# Revit family: ONRB - 1-6 door - All
name_source: partatom
category: Mechanical Equipment
units: mm (PartAtom-declared; Revit-internal decimal feet)

## family parameters
Always vertical = Yes
Cut with Voids When Loaded = No
OmniClass Number = 23.40.40.11.17
OmniClass Title = Refrigerated Cases
Part Type = Normal
Room Calculation Point = No
Round Connector Dimension = Use Radius
Shared = No
Work Plane-Based = Yes

## types (10) — shared parameters
20" Shelf = No
22" Shelf = Yes
Application Discipline = Beverage
BTUH Conventional = 549
BTUH Parallel = 519
Certifications = NSF 7, UL471, CSA
DATE = 01/29/2016
Default Elevation = 48"
Defrosts Per Day_2 = 4
Description = Narrow Reach-In Merchandiser
Discharge Air (°F) = 38 °F
Discharge Air Velocity (FPM) = 380 (FPM)
EQUIPMENT DESCRIPTION = Narrow Reach-In Merchandiser
EQUIPMENT MARK = ONRB
Evaporator (°F) = 34 °F
GLASS = Glass
Height = 81"
Item Description = Narrow Reach-In Merchandiser
Keynote = ONRB
Legend Number = ONRB
Manufacturer = HILL PHOENIX
Model = ONRB
NUMBER FOR GUIDLINES AND CONTROL ORGANIZATION = 1
PAINTED METAL EXTERIOR = CHARCOAL BROWN
Size of Door = 30"
Solid End LH = Yes
Superheat Set Point @ Bulb (°F) = 6-8 °F
Timed-Off Defrost Fail-Safe (Min) = 30 (Min)
Timed-Off Defrost Termination Temp_2 = 47°F
Type of Door Swing = A-Swing
URL = http://www.hillphoenix.com
Vista Optimax Pro Amps = 0 A
Vista Optimax Pro Watts = 0 W
Width = 34 7/8"
zero-valued in all types: NUMBER FOR ELECTRICAL DATA

## per-type parameters (varying)
| type | 101 Amps | 101 Watts | CENTER LINE & DRAIN | Crossfire/Polaris Amps | Crossfire/Polaris Watts | DOOR CONFIGURATION | Eliminaator Amps | Eliminaator Watts | GE Immersion Amps | GE Immersion Watts | High Efficiency Amps | High Efficiency Watts | Length | NUMBER FOR LIGHTING DATA | NUMBER OF DOORS | Number of Fans per Case | Optimax Pro Amps | Optimax Pro Watts | Solid End LH1 | Solid End RH | Solid End RH1 | Vista-C/60 Amps | Vista-C/60 Watts |
| 5 Door - Beverage | 1 A | 127 W | 90" | 1 A | 90 W | MASTER DOOR : 30" X 64 3/8" 6 DOOR A SWING (LEFT OPENING) | 1 A | 127 W | 1 A | 96 W | 1 A | 158 W | 180" | 6 | 6 | 6 | 1 A | 61 W | No | Yes | No | 1 A | 135 W |
| 6 Door - Beverage | 1 A | 127 W | 90" | 1 A | 90 W | MASTER DOOR : 30" X 64 3/8" 6 DOOR A SWING (LEFT OPENING) | 1 A | 127 W | 1 A | 96 W | 1 A | 158 W | 180" | 6 | 6 | 6 | 1 A | 61 W | Yes | No | Yes | 1 A | 135 W |
| 1 Door - Beverage | 0 A | 19 W | 15 1/2" | 0 A | 15 W | MASTER DOOR : 31" X 64 3/8" 1 DOOR A SWING (LEFT OPENING) | 0 A | 19 W | 0 A | 16 W | 0 A | 26 W | 31" | 1 | 1 | 1 | 0 A | 10 W | No | Yes | No | 0 A | 24 W |
| 2 DR | 0 A | 19 W | 30" | 0 A | 15 W | MASTER DOOR : 30" X 64 3/8" 2 DOOR A SWING (LEFT OPENING) | 0 A | 19 W | 0 A | 16 W | 0 A | 26 W | 60" | 1 | 1 | 1 | 0 A | 10 W | No | Yes | No | 0 A | 24 W |
| 3DR | 0 A | 19 W | 45" | 0 A | 15 W | MASTER DOOR : 30" X 64 3/8" 3 DOOR A SWING (LEFT OPENING) | 0 A | 19 W | 0 A | 16 W | 0 A | 26 W | 90" | 1 | 1 | 1 | 0 A | 10 W | No | Yes | No | 0 A | 24 W |
| 4DR | 0 A | 19 W | 60" | 0 A | 15 W | MASTER DOOR : 30" X 64 3/8" 4 DOOR A SWING (LEFT OPENING) | 0 A | 19 W | 0 A | 16 W | 0 A | 26 W | 120" | 1 | 1 | 1 | 0 A | 10 W | No | Yes | No | 0 A | 24 W |
| 4' | 0 A | 19 W | 24" | 0 A | 15 W | MASTER DOOR : 24" X 64 3/8" 2 DOOR B SWING | 0 A | 19 W | 0 A | 16 W | 0 A | 26 W | 48" | 1 | 1 | 1 | 0 A | 10 W | No | Yes | No | 0 A | 24 W |
| 6' | 0 A | 19 W | 36" | 0 A | 15 W | MASTER DOOR : 24" X 64 3/8" 3 DOOR B SWING (LEFT OPENING END) | 0 A | 19 W | 0 A | 16 W | 0 A | 26 W | 72" | 1 | 1 | 1 | 0 A | 10 W | No | Yes | No | 0 A | 24 W |
| 8' | 0 A | 19 W | 48" | 0 A | 15 W | MASTER DOOR : 24" X 64 3/8" 4 DOOR B SWING | 0 A | 19 W | 0 A | 16 W | 0 A | 26 W | 96" | 1 | 1 | 1 | 0 A | 10 W | No | Yes | No | 0 A | 24 W |
| 12' | 0 A | 19 W | 72" | 0 A | 15 W | MASTER DOOR : 24" X 64 3/8" 6 DOOR B SWING | 0 A | 19 W | 0 A | 16 W | 0 A | 26 W | 144" | 1 | 1 | 1 | 0 A | 10 W | No | Yes | No | 0 A | 24 W |

## geometry (parser evidence)
native form markers: Blend x8, Sweep x26
no freeform markers — native parametric forms only
